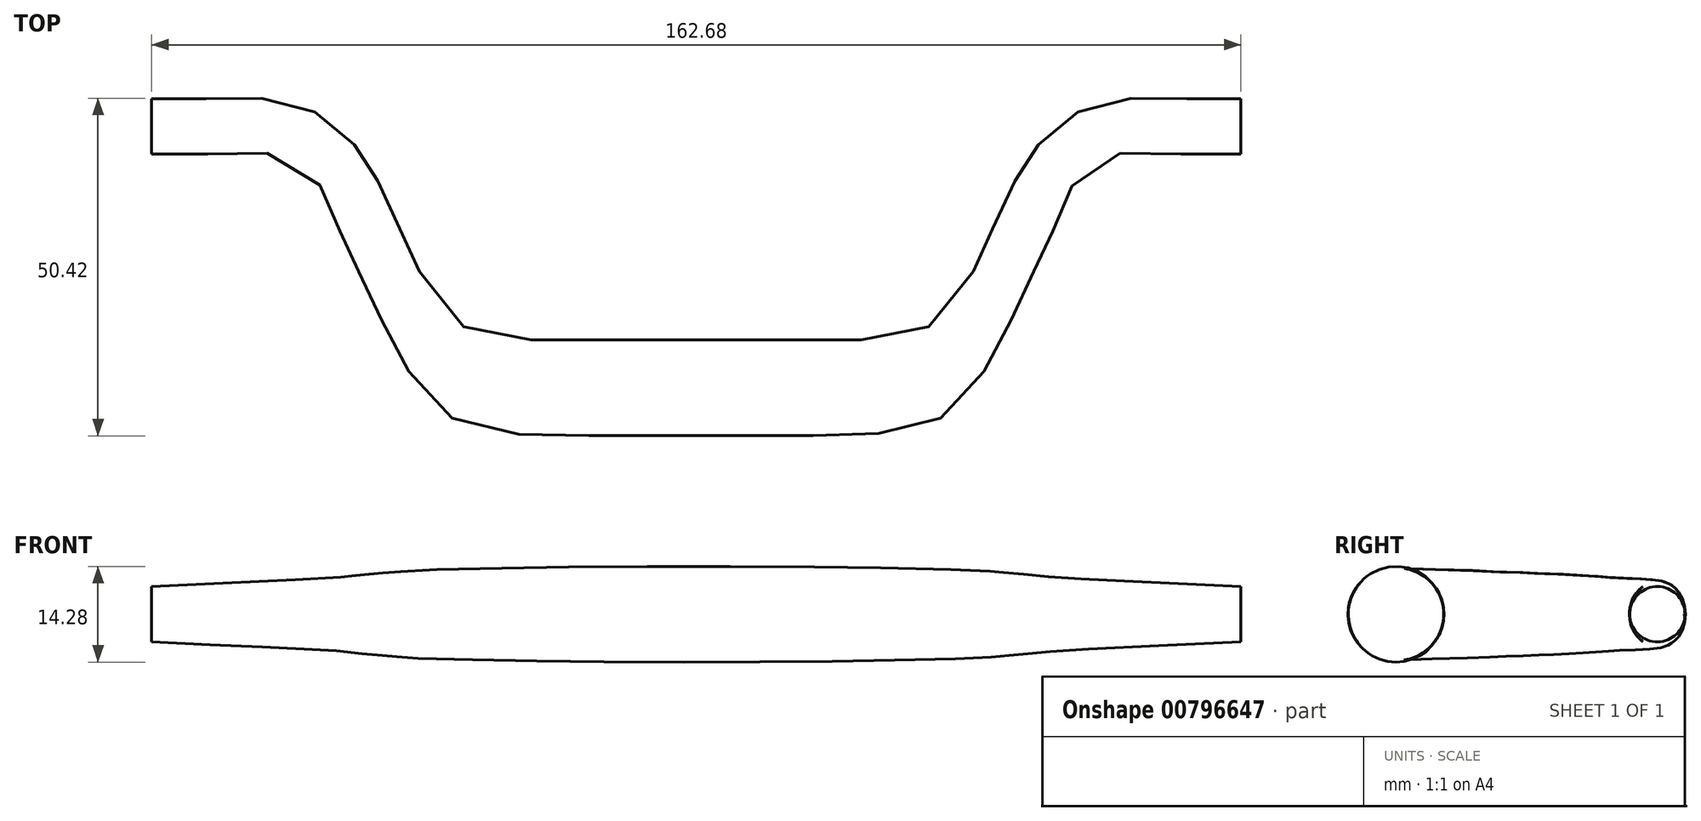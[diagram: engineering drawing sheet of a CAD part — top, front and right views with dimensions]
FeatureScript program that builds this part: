
annotation { "Feature Type Name" : "Feature", "Feature Type Description" : "" }
export const myFeature = defineFeature(function(context is Context, id is Id, definition is map)
    precondition{}
    {
        {
            var Q0;
            Q0=qCreatedBy(makeId("Right.planeOp"),FACE);
            cPlane(context, id + "F0", {"entities" : qUnion([Q0]), "cplaneType" : CPlaneType.OFFSET, "offset" : 81.34 * mm, "width" : 152.4 * mm, "height" : 152.4 * mm});
        }
        {
            var Q0;
            Q0=qCreatedBy(makeId("Right.planeOp"),FACE);
            cPlane(context, id + "F1", {"entities" : qUnion([Q0]), "cplaneType" : CPlaneType.OFFSET, "offset" : 81.34 * mm, "oppositeDirection" : true, "width" : 152.4 * mm, "height" : 152.4 * mm});
        }
        {
            var Q0;
            Q0=qCreatedBy(id+"F0.planeOp",FACE);
            var sketch = newSketch(context, id + "F2", { "sketchPlane" : qUnion([Q0])});
            skCircle(sketch, "E0", {"center": v(0, 0) * mm, "radius": 4.13 * mm});
            skSolve(sketch);
        }
        {
            var Q0;
            Q0=qCreatedBy(id+"F1.planeOp",FACE);
            var sketch = newSketch(context, id + "F3", { "sketchPlane" : qUnion([Q0])});
            skCircle(sketch, "E1.0", {"center": v(0, 0) * mm, "radius": 4.13 * mm});
            skSolve(sketch);
        }
        {
            var Q0;
            Q0=qCreatedBy(makeId("Right.planeOp"),FACE);
            var sketch = newSketch(context, id + "F4", { "sketchPlane" : qUnion([Q0])});
            skCircle(sketch, "E2", {"center": v(-39.02, 0) * mm, "radius": 7.14 * mm});
            skSolve(sketch);
        }
        {
            var Q0;
            Q0=qCreatedBy(makeId("Top.planeOp"),FACE);
            var sketch = newSketch(context, id + "F5", { "sketchPlane" : qUnion([Q0])});
            skFitSpline(sketch, "E3.0.2", {"points": [v(81.34, 4.13) * mm, v(76.68, 4.13) * mm, v(72.01, 4.13) * mm, v(67.12, 4.13) * mm, v(62.36, 4.16) * mm, v(57.84, 2.66) * mm, v(52.75, -1.05) * mm, v(51.34, -2.4) * mm, v(49.18, -5.18) * mm, v(48.36, -6.53) * mm, v(46.22, -11.1) * mm, v(44.76, -14.24) * mm, v(42.76, -18.53) * mm, v(42.25, -19.7) * mm, v(38.55, -26.63) * mm, v(32.89, -30.6) * mm, v(24.95, -31.86) * mm, v(23.41, -31.88) * mm, v(14.58, -31.88) * mm, v(7.29, -31.88) * mm, v(0, -31.88) * mm]});
            skFitSpline(sketch, "E3.0.3", {"points": [v(0, -31.88) * mm, v(-7.29, -31.88) * mm, v(-14.58, -31.88) * mm, v(-23.41, -31.88) * mm, v(-24.95, -31.86) * mm, v(-32.89, -30.6) * mm, v(-38.55, -26.63) * mm, v(-42.25, -19.7) * mm, v(-42.76, -18.53) * mm, v(-44.76, -14.24) * mm, v(-46.22, -11.1) * mm, v(-48.36, -6.53) * mm, v(-49.18, -5.18) * mm, v(-51.34, -2.4) * mm, v(-52.75, -1.05) * mm, v(-57.84, 2.66) * mm, v(-62.36, 4.16) * mm, v(-67.12, 4.13) * mm, v(-72.01, 4.13) * mm, v(-76.68, 4.13) * mm, v(-81.34, 4.13) * mm]});
            skSolve(sketch);
        }
        {
            var Q0;
            Q0=qCreatedBy(makeId("Top.planeOp"),FACE);
            var sketch = newSketch(context, id + "F6", { "sketchPlane" : qUnion([Q0])});
            skFitSpline(sketch, "E4.0.0", {"points": [v(0, -46.16) * mm, v(7.6, -46.16) * mm, v(15.2, -46.16) * mm, v(24.4, -46.16) * mm, v(26, -46.01) * mm, v(34.2, -44.46) * mm, v(40.1, -40.57) * mm, v(44.61, -33.84) * mm, v(45.26, -32.7) * mm, v(47.34, -28.23) * mm, v(48.87, -24.96) * mm, v(51.1, -20.19) * mm, v(51.8, -18.68) * mm, v(53.39, -15.27) * mm, v(54.28, -13.37) * mm, v(57.16, -7.18) * mm, v(61.57, -4.22) * mm, v(66.52, -4.13) * mm, v(71.62, -4.13) * mm, v(76.48, -4.13) * mm, v(81.34, -4.13) * mm]});
            skFitSpline(sketch, "E4.0.5", {"points": [v(0, -46.16) * mm, v(-7.6, -46.16) * mm, v(-15.2, -46.16) * mm, v(-24.4, -46.16) * mm, v(-26, -46.01) * mm, v(-34.2, -44.46) * mm, v(-40.1, -40.57) * mm, v(-44.61, -33.84) * mm, v(-45.26, -32.7) * mm, v(-47.34, -28.23) * mm, v(-48.87, -24.96) * mm, v(-51.1, -20.19) * mm, v(-51.8, -18.68) * mm, v(-53.39, -15.27) * mm, v(-54.28, -13.37) * mm, v(-57.16, -7.18) * mm, v(-61.57, -4.22) * mm, v(-66.52, -4.13) * mm, v(-71.62, -4.13) * mm, v(-76.48, -4.13) * mm, v(-81.34, -4.13) * mm]});
            skSolve(sketch);
        }
        {
            var Q0;
            Q0=makeQuery(id+"F2.imprint","IMPRINT",FACE,{"disambiguationData":[TD([[makeQuery(id+"F2.imprint","IMPRINT",EDGE,{"derivedFrom":sQuery(id+"F2.wireOp",EDGE,"E0")}),1.0]])]});
            var Q1;
            Q1=makeQuery(id+"F4.imprint","IMPRINT",FACE,{"disambiguationData":[TD([[makeQuery(id+"F4.imprint","IMPRINT",EDGE,{"derivedFrom":sQuery(id+"F4.wireOp",EDGE,"E2")}),1.0]])]});
            var Q2;
            Q2=makeQuery(id+"F3.imprint","IMPRINT",FACE,{"disambiguationData":[TD([[makeQuery(id+"F3.imprint","IMPRINT",EDGE,{"derivedFrom":sQuery(id+"F3.wireOp",EDGE,"E1.0")}),1.0]])]});
            var Q3;
            Q3=qBodyType(qCreatedBy(id+"F5",EDGE),BodyType.WIRE);
            var Q4;
            Q4=qBodyType(qCreatedBy(id+"F6",EDGE),BodyType.WIRE);
            loft(context, id + "F7", {"addGuides" : true, "sheetProfilesArray" : [{ "sheetProfileEntities" : qUnion([Q0]) }, { "sheetProfileEntities" : qUnion([Q1]) }, { "sheetProfileEntities" : qUnion([Q2]) }], "guidesArray" : [{ "guideEntities" : qUnion([Q3]), "guideDerivativeType" : LoftGuideDerivativeType.DEFAULT, "guideDerivativeMagnitude" : 1 }, { "guideEntities" : qUnion([Q4]), "guideDerivativeType" : LoftGuideDerivativeType.DEFAULT, "guideDerivativeMagnitude" : 1 }]});
        }
    });
